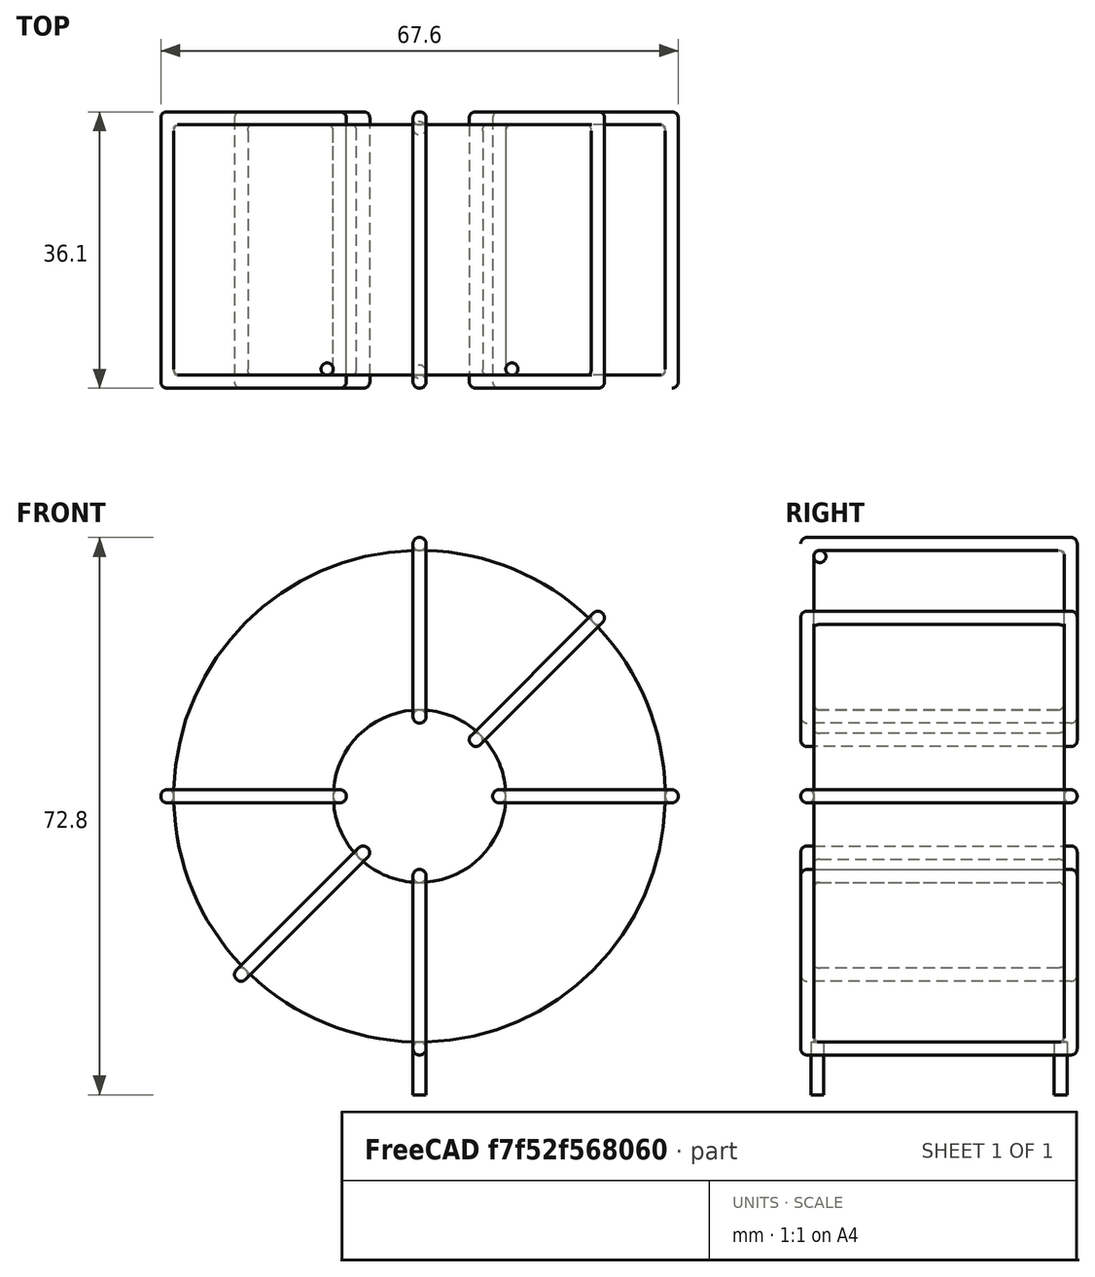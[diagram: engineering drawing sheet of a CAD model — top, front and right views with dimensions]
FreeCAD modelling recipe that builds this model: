
FCSTD DOCUMENT  (FreeCAD 0.16R6703 (Git))
Label: L_Toroid_Vertical_L67.6mm_W36.1mm_P31.80mm_Vishay_TJ9
License: All rights reserved
LicenseURL: http://en.wikipedia.org/wiki/All_rights_reserved
objects: Sketcher::SketchObject×6, PartDesign::Pad×6, PartDesign::Fillet×5, Spreadsheet::Sheet×1
note: 23 computed .brp shape members not serialized (recipe doc carries the construction recipe); baked Part::Feature solids carry a one-line shape summary decoded from their .brp

FEATURE [Spreadsheet::Sheet] Spreadsheet  label="dimensions"
  cells = A1=Wx; B1(Wx)=67.59999999999999; C1(WW)=22.53333333333333; D1=67.59999999999999; A2=Wy; B2(Wy)=36.1; D2=36.1; A3=RM; B3(RMx)=31.8; C3(RMy)=0; A4=d_wire; B4(d_wire)=1.7; A5=H; B5(H)=67.59999999999999; A6=offsetx; B6(offsetx)=33.8
FEATURE [Sketcher::SketchObject] Sketch
  Placement = pos=(0,-15.9,0) rot=(1,0,0;1.5708rad)
  expr: Placement.Base.y = -Spreadsheet.RMx / 2
  expr: Constraints[0] = Spreadsheet.Wx / 2 - Spreadsheet.d_wire
  expr: Constraints[4] = Spreadsheet.WW / 2
  expr: Constraints[2] = Spreadsheet.Wx / 2 + Spreadsheet.d_wire + 0.5
  sketch-geometry (2):
    g0: Circle CenterX=0 CenterY=36 CenterZ=0 NormalX=0 NormalY=0 NormalZ=1 Radius=32.1
    g1: Circle CenterX=0 CenterY=36 CenterZ=0 NormalX=0 NormalY=0 NormalZ=1 Radius=11.2667
  constraints (5):
    c: Radius(g0) = 32.1
    c: DistanceX(g-1,g0) = 0
    c: DistanceY(g-1,g0) = 36
    c: Coincident(g1,g0)
    c: Radius(g1) = 11.2667
FEATURE [PartDesign::Pad] Pad
  Length = 32.7
  Length2 = 100
  Midplane = true
  Placement = pos=(0,-15.9,0) rot=(1,0,0;1.5708rad)
  Sketch = -> Sketch
  Type = 0
  expr: Length = Spreadsheet.Wy - 2 * Spreadsheet.d_wire
FEATURE [Sketcher::SketchObject] Sketch001
  Placement = pos=(0,0,2.2) rot=(0,0,1;0rad)
  expr: Placement.Base.z = 0.5 + Spreadsheet.d_wire
  expr: Constraints[4] = Spreadsheet.RMy
  expr: Constraints[2] = -Spreadsheet.RMx
  expr: Constraints[1] = Spreadsheet.d_wire / 2
  sketch-geometry (2):
    g0: Circle CenterX=0 CenterY=0 CenterZ=0 NormalX=0 NormalY=0 NormalZ=1 Radius=0.85
    g1: Circle CenterX=0 CenterY=-31.8 CenterZ=0 NormalX=0 NormalY=0 NormalZ=1 Radius=0.85
  constraints (5):
    c: Equal(g0,g1)
    c: Radius(g0) = 0.85
    c: DistanceY(g-1,g1) = -31.8
    c: Coincident(g0,g-1)
    c: DistanceX(g-1,g1) = 0
FEATURE [PartDesign::Pad] Pad001
  Length = 1.7
  Length2 = 5.2
  Placement = pos=(0,0,2.2) rot=(0,0,1;0rad)
  Reversed = true
  Sketch = -> Sketch001
  Type = 4
  expr: Length2 = 3.5 + Spreadsheet.d_wire
  expr: Length = Spreadsheet.d_wire
FEATURE [PartDesign::Fillet] Fillet
  Base = -> Pad [Edge6,Edge3,Edge2]
  Placement = pos=(0,-15.9,0) rot=(1,0,0;1.5708rad)
  Radius = 0.5
FEATURE [Sketcher::SketchObject] Sketch003
  Placement = pos=(0,2.15,36) rot=(1,0,0;3.14159rad)
  expr: Constraints[18] = Spreadsheet.d_wire
  expr: Constraints[16] = Spreadsheet.d_wire
  expr: Constraints[19] = Spreadsheet.d_wire
  expr: Constraints[17] = Spreadsheet.d_wire
  expr: Placement.Base.y = -1 * (Spreadsheet.RMx - Spreadsheet.Wy) / 2
  expr: Constraints[21] = (Spreadsheet.Wx - Spreadsheet.WW) / 2 - Spreadsheet.d_wire
  expr: Constraints[22] = Spreadsheet.Wx / 2 - Spreadsheet.d_wire
  expr: Constraints[43] = Spreadsheet.d_wire
  expr: Constraints[48] = Spreadsheet.Wx - Spreadsheet.d_wire * 2
  expr: Constraints[49] = Spreadsheet.Wy
  expr: Placement.Base.z = Spreadsheet.Wx / 2 + Spreadsheet.d_wire + 0.5
  sketch-geometry (16):
    g0: LineSegment StartX=-9.56667 StartY=0 StartZ=0 EndX=-33.8 EndY=0 EndZ=0
    g1: LineSegment StartX=-33.8 StartY=0 StartZ=0 EndX=-33.8 EndY=36.1 EndZ=0
    g2: LineSegment StartX=-33.8 StartY=36.1 StartZ=0 EndX=-9.56667 EndY=36.1 EndZ=0
    g3: LineSegment StartX=-9.56667 StartY=36.1 StartZ=0 EndX=-9.56667 EndY=0 EndZ=0
    g4: LineSegment StartX=-32.1 StartY=34.4 StartZ=0 EndX=-11.2667 EndY=34.4 EndZ=0
    g5: LineSegment StartX=-11.2667 StartY=34.4 StartZ=0 EndX=-11.2667 EndY=1.7 EndZ=0
    g6: LineSegment StartX=-11.2667 StartY=1.7 StartZ=0 EndX=-32.1 EndY=1.7 EndZ=0
    g7: LineSegment StartX=-32.1 StartY=1.7 StartZ=0 EndX=-32.1 EndY=34.4 EndZ=0
    g8: LineSegment StartX=9.56667 StartY=36.1 StartZ=0 EndX=33.8 EndY=36.1 EndZ=0
    g9: LineSegment StartX=33.8 StartY=36.1 StartZ=0 EndX=33.8 EndY=0 EndZ=0
    g10: LineSegment StartX=33.8 StartY=0 StartZ=0 EndX=9.56667 EndY=0 EndZ=0
    g11: LineSegment StartX=9.56667 StartY=0 StartZ=0 EndX=9.56667 EndY=36.1 EndZ=0
    g12: LineSegment StartX=11.2667 StartY=34.4 StartZ=0 EndX=32.1 EndY=34.4 EndZ=0
    g13: LineSegment StartX=32.1 StartY=34.4 StartZ=0 EndX=32.1 EndY=1.7 EndZ=0
    g14: LineSegment StartX=32.1 StartY=1.7 StartZ=0 EndX=11.2667 EndY=1.7 EndZ=0
    g15: LineSegment StartX=11.2667 StartY=1.7 StartZ=0 EndX=11.2667 EndY=34.4 EndZ=0
  constraints (50):
    c: Horizontal(g0)
    c: Coincident(g1,g0)
    c: Vertical(g1)
    c: Coincident(g2,g1)
    c: Horizontal(g2)
    c: Coincident(g3,g2)
    c: Coincident(g3,g0)
    c: Vertical(g3)
    c: Coincident(g4,g5)
    c: Coincident(g5,g6)
    c: Coincident(g6,g7)
    c: Coincident(g7,g4)
    c: Horizontal(g4)
    c: Horizontal(g6)
    c: Vertical(g5)
    c: Vertical(g7)
    c: DistanceX(g1,g4) = 1.7
    c: DistanceY(g4,g1) = 1.7
    c: DistanceX(g5,g0) = 1.7
    c: DistanceY(g0,g5) = 1.7
    c: DistanceY(g-1,g0) = 0
    c: DistanceX(g6,g6) = 20.8333
    c: DistanceX(g6,g-1) = 32.1
    c: Coincident(g8,g9)
    c: Coincident(g9,g10)
    c: Coincident(g10,g11)
    c: Coincident(g11,g8)
    c: Horizontal(g8)
    c: Horizontal(g10)
    c: Vertical(g9)
    c: Vertical(g11)
    c: Coincident(g12,g13)
    c: Coincident(g13,g14)
    c: Coincident(g14,g15)
    c: Coincident(g15,g12)
    c: Horizontal(g12)
    c: Horizontal(g14)
    c: Vertical(g13)
    c: Vertical(g15)
    c: DistanceY(g8,g2) = 0
    c: DistanceY(g10,g0) = 0
    c: DistanceY(g14,g5) = 0
    c: DistanceY(g12,g4) = 0
    c: DistanceX(g8,g12) = 1.7
    c: Equal(g8,g2)
    c: Equal(g12,g4)
    c: Equal(g9,g1)
    c: Equal(g13,g7)
    c: DistanceX(g4,g12) = 64.2
    c: DistanceY(g0,g1) = 36.1
FEATURE [PartDesign::Pad] Pad002
  Length = 1.7
  Length2 = 100
  Midplane = true
  Placement = pos=(0,2.15,36) rot=(1,0,0;3.14159rad)
  Sketch = -> Sketch003
  Type = 0
  expr: Length = Spreadsheet.d_wire
FEATURE [PartDesign::Fillet] Fillet001
  Base = -> Pad002 [Edge38,Edge41,Edge42,Edge43,Edge29,Edge32,Edge33,Edge34,Edge25,Edge35,Edge36,Edge13,Edge14,Edge15,Edge16,Edge17,Edge18,Edge19,Edge1,Edge2,Edge3,Edge4,Edge5,Edge6,Edge7,Edge37,Edge39,Edge40,Edge20,Edge23,Edge24,Edge21,Edge22,Edge8,Edge9,Edge10,Edge11,Edge12,Edge26,Edge27,+8 more]
  Placement = pos=(0,2.15,36) rot=(1,0,0;3.14159rad)
  Radius = 0.799
  expr: Radius = Spreadsheet.d_wire * 0.47
FEATURE [Sketcher::SketchObject] Sketch004
  Placement = pos=(0,2.15,36) rot=(0.92388,0,0.382683;3.14159rad)
  expr: Constraints[18] = Spreadsheet.d_wire
  expr: Constraints[16] = Spreadsheet.d_wire
  expr: Constraints[19] = Spreadsheet.d_wire
  expr: Constraints[17] = Spreadsheet.d_wire
  expr: Placement.Base.y = -1 * (Spreadsheet.RMx - Spreadsheet.Wy) / 2
  expr: Constraints[21] = (Spreadsheet.Wx - Spreadsheet.WW) / 2 - Spreadsheet.d_wire
  expr: Constraints[22] = Spreadsheet.Wx / 2 - Spreadsheet.d_wire
  expr: Constraints[43] = Spreadsheet.d_wire
  expr: Constraints[48] = Spreadsheet.Wx - 2 * Spreadsheet.d_wire
  expr: Constraints[49] = Spreadsheet.Wy
  expr: Placement.Base.z = Spreadsheet.Wx / 2 + Spreadsheet.d_wire + 0.5
  sketch-geometry (16):
    g0: LineSegment StartX=-9.56667 StartY=0 StartZ=0 EndX=-33.8 EndY=0 EndZ=0
    g1: LineSegment StartX=-33.8 StartY=0 StartZ=0 EndX=-33.8 EndY=36.1 EndZ=0
    g2: LineSegment StartX=-33.8 StartY=36.1 StartZ=0 EndX=-9.56667 EndY=36.1 EndZ=0
    g3: LineSegment StartX=-9.56667 StartY=36.1 StartZ=0 EndX=-9.56667 EndY=0 EndZ=0
    g4: LineSegment StartX=-32.1 StartY=34.4 StartZ=0 EndX=-11.2667 EndY=34.4 EndZ=0
    g5: LineSegment StartX=-11.2667 StartY=34.4 StartZ=0 EndX=-11.2667 EndY=1.7 EndZ=0
    g6: LineSegment StartX=-11.2667 StartY=1.7 StartZ=0 EndX=-32.1 EndY=1.7 EndZ=0
    g7: LineSegment StartX=-32.1 StartY=1.7 StartZ=0 EndX=-32.1 EndY=34.4 EndZ=0
    g8: LineSegment StartX=9.56667 StartY=36.1 StartZ=0 EndX=33.8 EndY=36.1 EndZ=0
    g9: LineSegment StartX=33.8 StartY=36.1 StartZ=0 EndX=33.8 EndY=0 EndZ=0
    g10: LineSegment StartX=33.8 StartY=0 StartZ=0 EndX=9.56667 EndY=0 EndZ=0
    g11: LineSegment StartX=9.56667 StartY=0 StartZ=0 EndX=9.56667 EndY=36.1 EndZ=0
    g12: LineSegment StartX=11.2667 StartY=34.4 StartZ=0 EndX=32.1 EndY=34.4 EndZ=0
    g13: LineSegment StartX=32.1 StartY=34.4 StartZ=0 EndX=32.1 EndY=1.7 EndZ=0
    g14: LineSegment StartX=32.1 StartY=1.7 StartZ=0 EndX=11.2667 EndY=1.7 EndZ=0
    g15: LineSegment StartX=11.2667 StartY=1.7 StartZ=0 EndX=11.2667 EndY=34.4 EndZ=0
  constraints (50):
    c: Horizontal(g0)
    c: Coincident(g1,g0)
    c: Vertical(g1)
    c: Coincident(g2,g1)
    c: Horizontal(g2)
    c: Coincident(g3,g2)
    c: Coincident(g3,g0)
    c: Vertical(g3)
    c: Coincident(g4,g5)
    c: Coincident(g5,g6)
    c: Coincident(g6,g7)
    c: Coincident(g7,g4)
    c: Horizontal(g4)
    c: Horizontal(g6)
    c: Vertical(g5)
    c: Vertical(g7)
    c: DistanceX(g1,g4) = 1.7
    c: DistanceY(g4,g1) = 1.7
    c: DistanceX(g5,g0) = 1.7
    c: DistanceY(g0,g5) = 1.7
    c: DistanceY(g-1,g0) = 0
    c: DistanceX(g6,g6) = 20.8333
    c: DistanceX(g6,g-1) = 32.1
    c: Coincident(g8,g9)
    c: Coincident(g9,g10)
    c: Coincident(g10,g11)
    c: Coincident(g11,g8)
    c: Horizontal(g8)
    c: Horizontal(g10)
    c: Vertical(g9)
    c: Vertical(g11)
    c: Coincident(g12,g13)
    c: Coincident(g13,g14)
    c: Coincident(g14,g15)
    c: Coincident(g15,g12)
    c: Horizontal(g12)
    c: Horizontal(g14)
    c: Vertical(g13)
    c: Vertical(g15)
    c: DistanceY(g8,g2) = 0
    c: DistanceY(g10,g0) = 0
    c: DistanceY(g14,g5) = 0
    c: DistanceY(g12,g4) = 0
    c: DistanceX(g8,g12) = 1.7
    c: Equal(g8,g2)
    c: Equal(g12,g4)
    c: Equal(g9,g1)
    c: Equal(g13,g7)
    c: DistanceX(g4,g12) = 64.2
    c: DistanceY(g0,g1) = 36.1
FEATURE [PartDesign::Pad] Pad003
  Length = 1.7
  Length2 = 100
  Midplane = true
  Placement = pos=(0,2.15,36) rot=(0.92388,0,0.382683;3.14159rad)
  Sketch = -> Sketch004
  Type = 0
  expr: Length = Spreadsheet.d_wire
FEATURE [PartDesign::Fillet] Fillet002
  Base = -> Pad003 [Edge38,Edge41,Edge42,Edge43,Edge29,Edge32,Edge33,Edge34,Edge25,Edge35,Edge36,Edge13,Edge14,Edge15,Edge16,Edge17,Edge18,Edge19,Edge1,Edge2,Edge3,Edge4,Edge5,Edge6,Edge7,Edge37,Edge39,Edge40,Edge20,Edge23,Edge24,Edge21,Edge22,Edge8,Edge9,Edge10,Edge11,Edge12,Edge26,Edge27,+8 more]
  Placement = pos=(0,2.15,36) rot=(0.92388,0,0.382683;3.14159rad)
  Radius = 0.799
  expr: Radius = Spreadsheet.d_wire * 0.47
FEATURE [Sketcher::SketchObject] Sketch005
  Placement = pos=(0,2.15,36) rot=(0.92388,0,-0.382683;3.14159rad)
  expr: Constraints[18] = Spreadsheet.d_wire
  expr: Constraints[16] = Spreadsheet.d_wire
  expr: Constraints[19] = Spreadsheet.d_wire
  expr: Constraints[17] = Spreadsheet.d_wire
  expr: Placement.Base.y = -1 * (Spreadsheet.RMx - Spreadsheet.Wy) / 2
  expr: Constraints[21] = (Spreadsheet.Wx - Spreadsheet.WW) / 2 - Spreadsheet.d_wire
  expr: Constraints[22] = Spreadsheet.Wx / 2 - Spreadsheet.d_wire
  expr: Constraints[43] = Spreadsheet.d_wire
  expr: Constraints[48] = Spreadsheet.Wx - 2 * Spreadsheet.d_wire
  expr: Constraints[49] = Spreadsheet.Wy
  expr: Placement.Base.z = Spreadsheet.Wx / 2 + Spreadsheet.d_wire + 0.5
  sketch-geometry (16):
    g0: LineSegment StartX=-9.56667 StartY=0 StartZ=0 EndX=-33.8 EndY=0 EndZ=0
    g1: LineSegment StartX=-33.8 StartY=0 StartZ=0 EndX=-33.8 EndY=36.1 EndZ=0
    g2: LineSegment StartX=-33.8 StartY=36.1 StartZ=0 EndX=-9.56667 EndY=36.1 EndZ=0
    g3: LineSegment StartX=-9.56667 StartY=36.1 StartZ=0 EndX=-9.56667 EndY=0 EndZ=0
    g4: LineSegment StartX=-32.1 StartY=34.4 StartZ=0 EndX=-11.2667 EndY=34.4 EndZ=0
    g5: LineSegment StartX=-11.2667 StartY=34.4 StartZ=0 EndX=-11.2667 EndY=1.7 EndZ=0
    g6: LineSegment StartX=-11.2667 StartY=1.7 StartZ=0 EndX=-32.1 EndY=1.7 EndZ=0
    g7: LineSegment StartX=-32.1 StartY=1.7 StartZ=0 EndX=-32.1 EndY=34.4 EndZ=0
    g8: LineSegment StartX=9.56667 StartY=36.1 StartZ=0 EndX=33.8 EndY=36.1 EndZ=0
    g9: LineSegment StartX=33.8 StartY=36.1 StartZ=0 EndX=33.8 EndY=0 EndZ=0
    g10: LineSegment StartX=33.8 StartY=0 StartZ=0 EndX=9.56667 EndY=0 EndZ=0
    g11: LineSegment StartX=9.56667 StartY=0 StartZ=0 EndX=9.56667 EndY=36.1 EndZ=0
    g12: LineSegment StartX=11.2667 StartY=34.4 StartZ=0 EndX=32.1 EndY=34.4 EndZ=0
    g13: LineSegment StartX=32.1 StartY=34.4 StartZ=0 EndX=32.1 EndY=1.7 EndZ=0
    g14: LineSegment StartX=32.1 StartY=1.7 StartZ=0 EndX=11.2667 EndY=1.7 EndZ=0
    g15: LineSegment StartX=11.2667 StartY=1.7 StartZ=0 EndX=11.2667 EndY=34.4 EndZ=0
  constraints (50):
    c: Horizontal(g0)
    c: Coincident(g1,g0)
    c: Vertical(g1)
    c: Coincident(g2,g1)
    c: Horizontal(g2)
    c: Coincident(g3,g2)
    c: Coincident(g3,g0)
    c: Vertical(g3)
    c: Coincident(g4,g5)
    c: Coincident(g5,g6)
    c: Coincident(g6,g7)
    c: Coincident(g7,g4)
    c: Horizontal(g4)
    c: Horizontal(g6)
    c: Vertical(g5)
    c: Vertical(g7)
    c: DistanceX(g1,g4) = 1.7
    c: DistanceY(g4,g1) = 1.7
    c: DistanceX(g5,g0) = 1.7
    c: DistanceY(g0,g5) = 1.7
    c: DistanceY(g-1,g0) = 0
    c: DistanceX(g6,g6) = 20.8333
    c: DistanceX(g6,g-1) = 32.1
    c: Coincident(g8,g9)
    c: Coincident(g9,g10)
    c: Coincident(g10,g11)
    c: Coincident(g11,g8)
    c: Horizontal(g8)
    c: Horizontal(g10)
    c: Vertical(g9)
    c: Vertical(g11)
    c: Coincident(g12,g13)
    c: Coincident(g13,g14)
    c: Coincident(g14,g15)
    c: Coincident(g15,g12)
    c: Horizontal(g12)
    c: Horizontal(g14)
    c: Vertical(g13)
    c: Vertical(g15)
    c: DistanceY(g8,g2) = 0
    c: DistanceY(g10,g0) = 0
    c: DistanceY(g14,g5) = 0
    c: DistanceY(g12,g4) = 0
    c: DistanceX(g8,g12) = 1.7
    c: Equal(g8,g2)
    c: Equal(g12,g4)
    c: Equal(g9,g1)
    c: Equal(g13,g7)
    c: DistanceX(g4,g12) = 64.2
    c: DistanceY(g0,g1) = 36.1
FEATURE [PartDesign::Pad] Pad004
  Length = 1.7
  Length2 = 100
  Midplane = true
  Placement = pos=(0,2.15,36) rot=(0.92388,0,-0.382683;3.14159rad)
  Sketch = -> Sketch005
  Type = 0
  expr: Length = Spreadsheet.d_wire
FEATURE [PartDesign::Fillet] Fillet003
  Base = -> Pad004 [Edge38,Edge41,Edge42,Edge43,Edge29,Edge32,Edge33,Edge34,Edge25,Edge35,Edge36,Edge13,Edge14,Edge15,Edge16,Edge17,Edge18,Edge19,Edge1,Edge2,Edge3,Edge4,Edge5,Edge6,Edge7,Edge37,Edge39,Edge40,Edge20,Edge23,Edge24,Edge21,Edge22,Edge8,Edge9,Edge10,Edge11,Edge12,Edge26,Edge27,+8 more]
  Placement = pos=(0,2.15,36) rot=(0.92388,0,-0.382683;3.14159rad)
  Radius = 0.799
  expr: Radius = Spreadsheet.d_wire * 0.47
FEATURE [Sketcher::SketchObject] Sketch006
  Placement = pos=(0,2.15,36) rot=(0.707107,0,0.707107;3.14159rad)
  expr: Constraints[18] = Spreadsheet.d_wire
  expr: Constraints[16] = Spreadsheet.d_wire
  expr: Constraints[19] = Spreadsheet.d_wire
  expr: Constraints[17] = Spreadsheet.d_wire
  expr: Placement.Base.y = -1 * (Spreadsheet.RMx - Spreadsheet.Wy) / 2
  expr: Constraints[21] = (Spreadsheet.Wx - Spreadsheet.WW) / 2 - Spreadsheet.d_wire
  expr: Constraints[22] = Spreadsheet.Wx / 2 - Spreadsheet.d_wire
  expr: Constraints[43] = Spreadsheet.d_wire
  expr: Constraints[48] = Spreadsheet.Wx - Spreadsheet.d_wire * 2
  expr: Constraints[49] = Spreadsheet.Wy
  expr: Placement.Base.z = Spreadsheet.Wx / 2 + Spreadsheet.d_wire + 0.5
  sketch-geometry (16):
    g0: LineSegment StartX=-9.56667 StartY=0 StartZ=0 EndX=-33.8 EndY=0 EndZ=0
    g1: LineSegment StartX=-33.8 StartY=0 StartZ=0 EndX=-33.8 EndY=36.1 EndZ=0
    g2: LineSegment StartX=-33.8 StartY=36.1 StartZ=0 EndX=-9.56667 EndY=36.1 EndZ=0
    g3: LineSegment StartX=-9.56667 StartY=36.1 StartZ=0 EndX=-9.56667 EndY=0 EndZ=0
    g4: LineSegment StartX=-32.1 StartY=34.4 StartZ=0 EndX=-11.2667 EndY=34.4 EndZ=0
    g5: LineSegment StartX=-11.2667 StartY=34.4 StartZ=0 EndX=-11.2667 EndY=1.7 EndZ=0
    g6: LineSegment StartX=-11.2667 StartY=1.7 StartZ=0 EndX=-32.1 EndY=1.7 EndZ=0
    g7: LineSegment StartX=-32.1 StartY=1.7 StartZ=0 EndX=-32.1 EndY=34.4 EndZ=0
    g8: LineSegment StartX=9.56667 StartY=36.1 StartZ=0 EndX=33.8 EndY=36.1 EndZ=0
    g9: LineSegment StartX=33.8 StartY=36.1 StartZ=0 EndX=33.8 EndY=0 EndZ=0
    g10: LineSegment StartX=33.8 StartY=0 StartZ=0 EndX=9.56667 EndY=0 EndZ=0
    g11: LineSegment StartX=9.56667 StartY=0 StartZ=0 EndX=9.56667 EndY=36.1 EndZ=0
    g12: LineSegment StartX=11.2667 StartY=34.4 StartZ=0 EndX=32.1 EndY=34.4 EndZ=0
    g13: LineSegment StartX=32.1 StartY=34.4 StartZ=0 EndX=32.1 EndY=1.7 EndZ=0
    g14: LineSegment StartX=32.1 StartY=1.7 StartZ=0 EndX=11.2667 EndY=1.7 EndZ=0
    g15: LineSegment StartX=11.2667 StartY=1.7 StartZ=0 EndX=11.2667 EndY=34.4 EndZ=0
  constraints (50):
    c: Horizontal(g0)
    c: Coincident(g1,g0)
    c: Vertical(g1)
    c: Coincident(g2,g1)
    c: Horizontal(g2)
    c: Coincident(g3,g2)
    c: Coincident(g3,g0)
    c: Vertical(g3)
    c: Coincident(g4,g5)
    c: Coincident(g5,g6)
    c: Coincident(g6,g7)
    c: Coincident(g7,g4)
    c: Horizontal(g4)
    c: Horizontal(g6)
    c: Vertical(g5)
    c: Vertical(g7)
    c: DistanceX(g1,g4) = 1.7
    c: DistanceY(g4,g1) = 1.7
    c: DistanceX(g5,g0) = 1.7
    c: DistanceY(g0,g5) = 1.7
    c: DistanceY(g-1,g0) = 0
    c: DistanceX(g6,g6) = 20.8333
    c: DistanceX(g6,g-1) = 32.1
    c: Coincident(g8,g9)
    c: Coincident(g9,g10)
    c: Coincident(g10,g11)
    c: Coincident(g11,g8)
    c: Horizontal(g8)
    c: Horizontal(g10)
    c: Vertical(g9)
    c: Vertical(g11)
    c: Coincident(g12,g13)
    c: Coincident(g13,g14)
    c: Coincident(g14,g15)
    c: Coincident(g15,g12)
    c: Horizontal(g12)
    c: Horizontal(g14)
    c: Vertical(g13)
    c: Vertical(g15)
    c: DistanceY(g8,g2) = 0
    c: DistanceY(g10,g0) = 0
    c: DistanceY(g14,g5) = 0
    c: DistanceY(g12,g4) = 0
    c: DistanceX(g8,g12) = 1.7
    c: Equal(g8,g2)
    c: Equal(g12,g4)
    c: Equal(g9,g1)
    c: Equal(g13,g7)
    c: DistanceX(g4,g12) = 64.2
    c: DistanceY(g0,g1) = 36.1
FEATURE [PartDesign::Pad] Pad005
  Length = 1.7
  Length2 = 100
  Midplane = true
  Placement = pos=(0,2.15,36) rot=(0.707107,0,0.707107;3.14159rad)
  Sketch = -> Sketch006
  Type = 0
  expr: Length = Spreadsheet.d_wire
FEATURE [PartDesign::Fillet] Fillet004
  Base = -> Pad005 [Edge38,Edge41,Edge42,Edge43,Edge29,Edge32,Edge33,Edge34,Edge25,Edge35,Edge36,Edge13,Edge14,Edge15,Edge16,Edge17,Edge18,Edge19,Edge1,Edge2,Edge3,Edge4,Edge5,Edge6,Edge7,Edge37,Edge39,Edge40,Edge20,Edge23,Edge24,Edge21,Edge22,Edge8,Edge9,Edge10,Edge11,Edge12,Edge26,Edge27,+8 more]
  Placement = pos=(0,2.15,36) rot=(0.707107,0,0.707107;3.14159rad)
  Radius = 0.799
  expr: Radius = Spreadsheet.d_wire * 0.47
